# Revit family: Electronics_Desono_Biamp_Two-Way-Pendant-Mount-Loudspeaker_P30DT
name_source: partatom
category: Communication Devices
units: mm (PartAtom-declared; Revit-internal decimal feet)

## family parameters
Cut with Voids When Loaded = No
Host = Face
Maintain Annotation Orientation = No
OmniClass Number = 23.85.10.11.14.14.14
OmniClass Title = Loudspeakers
Part Type = Normal
Room Calculation Point = No
Round Connector Dimension = Use Diameter
Shared = No

## types (2) — shared parameters
Compliance = ETL listed to comply with UL Std 1480A,Certifed to CSA C22.2#62368-1Suspension system and Gripple cable fasteners listed per UL1598 and UL2239, TUV and CSA Class 3426-01 and Class 3426-81.
Connector Description = Euroblock; Low Impedance 16 ohms, 70/100V operation
Continuous Power Handling Nominal Impedance = Passive - 28V - 50W @ 16 ohms (200W peak)
Controls = Power tap / low impedance selector switch
Default Elevation = 4' - 0"
Description = Desono™ P30DT Two-Way 4.25-Inch Pendant Mount Loudspeaker
Diameter = 0' - 9"
Height = 0' - 9"
Input Connection = 4-way Euroblock connector with permanent pass-through
Manufacturer = Biamp
Mounting Provisions = Two 5m (16.4 ft) wire suspension cables (one as primary support, one as a safety cable), of high tensile galvanized steel wire rope with integrated spring clips for attaching the cable to the bracket and Gripple cable fasteners.
Nominal Beamwidth  (H x V) = 120°, conical
Nominal Maximum SPL @ 1m = Passive - Peak 110dB - Continuous 104dB)
Nominal Sensitivity @ 1m = Passive - 1W 87dB - 2.83V 84dB)
Operating Environment = Indoor
Operating Mode = Passive
Operating Range (-10dB) = 75 Hz to 20 kHz
Product Documentation Link = https://downloads.biamp.com
Product Page URL = https://www.biamp.com
Product data url = https://www.bimobject.com
Protection = Self-resetting loudspeaker protection
Recommended Accessories = 75 Hz, 12dB/Oct High Pass
Recommended Amplifers = 50W - 100W @ 16 ohms, (28V - 40V)
Transducers = LF 1 x 4.25 (108 mm) coated paper cone HF 1 x 1 (25 mm) soft dome
Transformer = 70V: 30W, 15W, 7.5W, 3.75W, 1.75W; 100V: 30W, 15W, 7.5W, 3.75W
URL = https://www.biamp.com
Weight = 5.73 lb

## per-type parameters (varying)
| type | Bracket Material | Grill Material | Housing Material |
| P30DT W | Biamp - Metal - White | Biamp - Plastic - White(Grid) | Biamp - Plastic - White |
| P30DT B | Biamp - Metal - Black | Biamp - Plastic - Black(Grid) | Biamp - Plastic - Black |

note: column(s) folded — value = type name in every type: Model

## geometry (parser evidence)
native form markers: Sweep x2
no freeform markers — native parametric forms only
